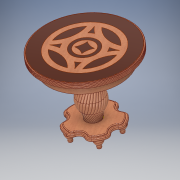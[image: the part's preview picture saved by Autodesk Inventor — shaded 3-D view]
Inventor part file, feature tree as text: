
AUTODESK INVENTOR PART (.ipt)
format: ipt  version: 2019 (Build 230136000, 136)  size: 6,526,464 bytes
history: native  units: mm
features: sketch x11, other x10, extrude x5, pattern_circular x4, projected_geometry x4, revolve x3, fillet x3, sweep x1
ambient origin geometry x8: Origin, YZ Plane, XZ Plane, XY Plane, X Axis, Y Axis, Z Axis, Center Point
bodies: Body1 (feature_tree), Body2 (feature_tree), Body3 (feature_tree), Body4 (feature_tree)
feature tree (41):
  revolve  "Вращение1"
  extrude  "Выдавливание5"  Depth=60.0mm
  pattern_circular  "Круговой массив2"  [2 undecoded]
  revolve  "Вращение3"
  fillet  "Сопряжение3"  Radius=75.0mm
  sketch  "Эскиз9"
  other  "РабПлоскость2"
  sketch  "Эскиз10"
  other  "РабПлоскость3"
  sketch  "Эскиз11"
  sweep  "Сдвиг1"
  pattern_circular  "Круговой массив3"  Angle=90.0deg  [1 undecoded]
  extrude  "Выдавливание2"  Depth=600.0mm
  pattern_circular  "Круговой массив1"  Count=35  [1 undecoded]
  extrude  "Выдавливание3"  Depth=50.0mm
  fillet  "Сопряжение1"  Radius=200.0mm
  extrude  "Выдавливание4"  Depth=40.0mm
  other  "РабПлоскость1"
  revolve  "Вращение2"
  fillet  "Сопряжение2"  Radius=80.0mm
  pattern_circular  "Круговой массив6"  [2 undecoded]
  extrude  "Выдавливание6"  Depth=60.0mm
  sketch  "Эскиз2"
  sketch  "Эскиз3"
  projected_geometry  "Спроецированная петля2"
  sketch  "Эскиз4"
  projected_geometry  "Спроецированная петля3"
  sketch  "Эскиз5"
  projected_geometry  "Спроецированная петля5"
  other  "Твердое тело3"
  sketch  "Эскиз6"
  sketch  "Эскиз7"
  projected_geometry  "Спроецированная петля6"
  other  "Твердое тело4"
  sketch  "Эскиз8"
  sketch  "Эскиз15"
  other  "Инкрустация"
  other  "Проецирование ребер1"
  other  "Проецирование ребер2"
  other  "Проецирование ребер3"
  other  "Проецирование ребер4"
note: 6 required parameter values undecoded (feature->parameter linkage not recoverable at this tier; creation-order binding heuristic only, values carry confidence <= 0.55)
